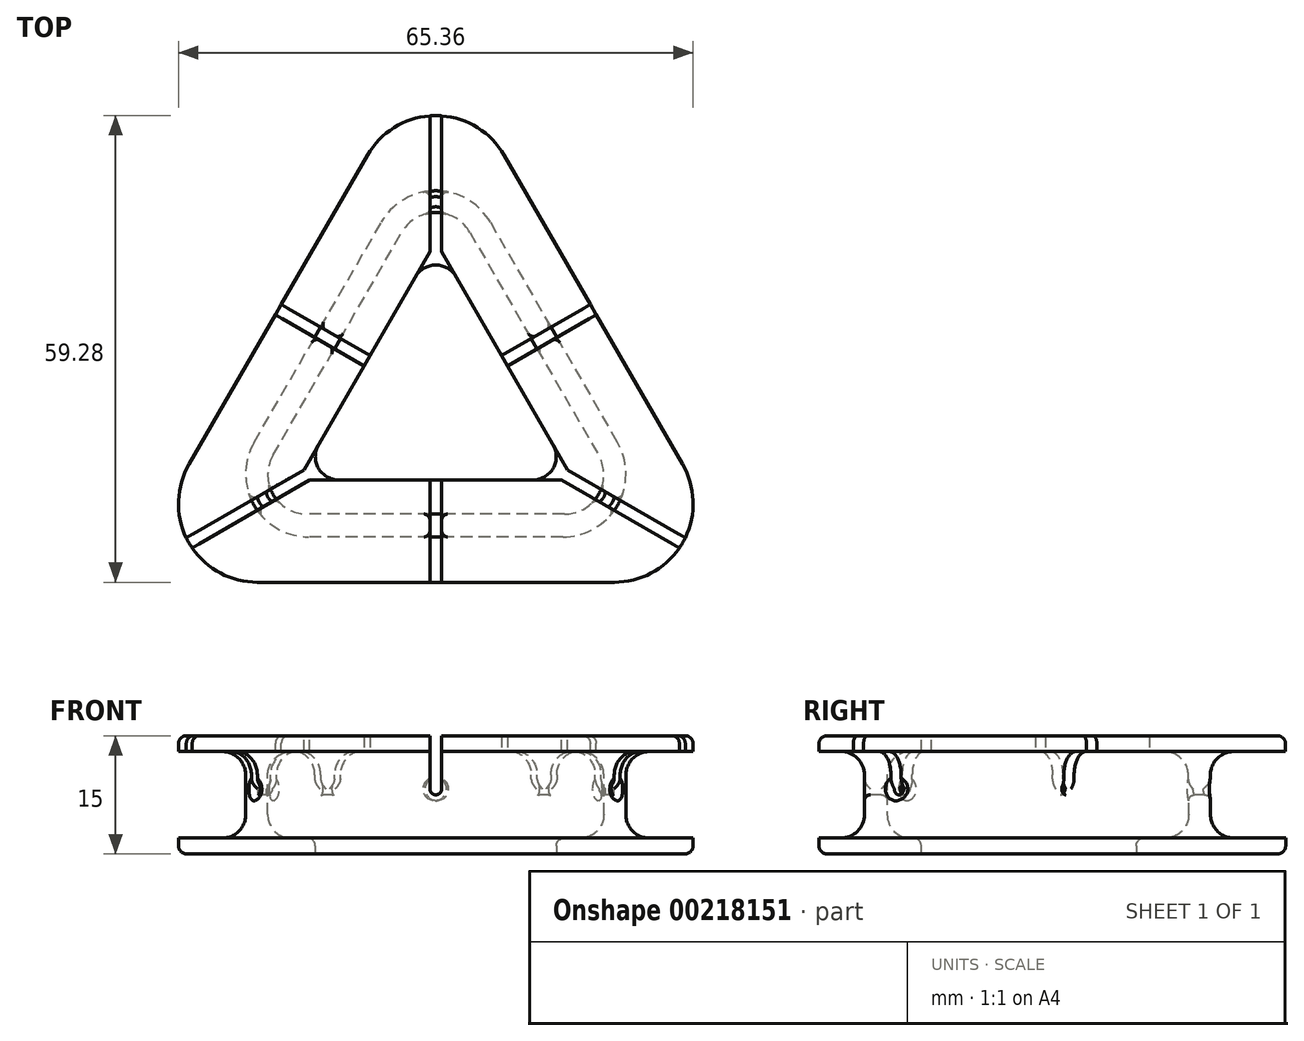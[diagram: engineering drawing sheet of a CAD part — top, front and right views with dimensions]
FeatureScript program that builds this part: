
annotation { "Feature Type Name" : "Feature", "Feature Type Description" : "" }
export const myFeature = defineFeature(function(context is Context, id is Id, definition is map)
    precondition{}
    {
        {
            var Q0;
            Q0=qCreatedBy(makeId("Top.planeOp"),FACE);
            var sketch = newSketch(context, id + "F0", { "sketchPlane" : qUnion([Q0])});
            skCircle(sketch, "E0.cCircle", {"center": v(0, 0) * mm, "radius": 23.1 * mm, "construction": true});
            skLineSegment(sketch, "E0.0", {"start": v(40, -23.1) * mm, "end": v(-40, -23.1) * mm});
            skLineSegment(sketch, "E0.1", {"start": v(-40, -23.1) * mm, "end": v(0, 46.19) * mm});
            skLineSegment(sketch, "E0.2", {"start": v(0, 46.19) * mm, "end": v(40, -23.1) * mm});
            skPoint(sketch, "E0.0.midPoint", {"position": v(0, -23.1) * mm});
            skSolve(sketch);
        }
        {
            var Q0;
            Q0 = qSketchRegion(id + "F0", true);
            extrude(context, id + "F1", {"entities" : qUnion([Q0]), "offsetDistance" : 25 * mm, "depth" : 15 * mm, "symmetric" : true});
        }
        {
            var Q0;
            Q0=makeQuery(id+"F1.opExtrude","SWEPT_EDGE",EDGE,{"disambiguationData":[OSD([sQuery(id+"F0.wireOp",EDGE,"E0.1"),sQuery(id+"F0.wireOp",EDGE,"E0.2")])]});
            var Q1;
            Q1=makeQuery(id+"F1.opExtrude","SWEPT_EDGE",EDGE,{"disambiguationData":[OSD([sQuery(id+"F0.wireOp",EDGE,"E0.0"),sQuery(id+"F0.wireOp",EDGE,"E0.1")])]});
            var Q2;
            Q2=makeQuery(id+"F1.opExtrude","SWEPT_EDGE",EDGE,{"disambiguationData":[OSD([sQuery(id+"F0.wireOp",EDGE,"E0.0"),sQuery(id+"F0.wireOp",EDGE,"E0.2")])]});
            fillet(context, id + "F2", {"entities" : qUnion([Q0, Q1, Q2]), "radius" : 10 * mm, "tangentPropagation" : true, "allowEdgeOverflow" : false});
        }
        {
            var Q0;
            Q0=qCreatedBy(makeId("Top.planeOp"),FACE);
            var sketch = newSketch(context, id + "F3", { "sketchPlane" : qUnion([Q0])});
            skCircle(sketch, "E1.cCircle", {"center": v(0, 0) * mm, "radius": 17.32 * mm, "construction": true});
            skLineSegment(sketch, "E1.0", {"start": v(0, 34.64) * mm, "end": v(30, -17.32) * mm});
            skLineSegment(sketch, "E1.1", {"start": v(30, -17.32) * mm, "end": v(-30, -17.32) * mm});
            skLineSegment(sketch, "E1.2", {"start": v(-30, -17.32) * mm, "end": v(0, 34.64) * mm});
            skPoint(sketch, "E1.0.midPoint", {"position": v(15, 8.66) * mm});
            skCircle(sketch, "E2.cCircle", {"center": v(0, 0) * mm, "radius": 23.1 * mm, "construction": true});
            skLineSegment(sketch, "E2.0", {"start": v(40, -23.1) * mm, "end": v(-40, -23.1) * mm});
            skLineSegment(sketch, "E2.1", {"start": v(-40, -23.1) * mm, "end": v(0, 46.19) * mm});
            skLineSegment(sketch, "E2.2", {"start": v(0, 46.19) * mm, "end": v(40, -23.1) * mm});
            skPoint(sketch, "E2.0.midPoint", {"position": v(0, -23.1) * mm});
            skSolve(sketch);
        }
        {
            var Q0;
            Q0=makeQuery(id+"F3.imprint","IMPRINT",FACE,{"disambiguationData":[TD([[makeQuery(id+"F3.imprint","IMPRINT",EDGE,{"derivedFrom":sQuery(id+"F3.wireOp",EDGE,"E1.0")}),1.0]])]});
            extrude(context, id + "F4", {"entities" : qUnion([Q0]), "operationType" : NewBodyOperationType.REMOVE, "oppositeDirection" : true, "depth" : 11 * mm, "symmetric" : true});
        }
        {
            var Q0;
            Q0=qCreatedBy(makeId("Top.planeOp"),FACE);
            var sketch = newSketch(context, id + "F5", { "sketchPlane" : qUnion([Q0])});
            skCircle(sketch, "E3.cCircle", {"center": v(0, 0) * mm, "radius": 14.43 * mm, "construction": true});
            skLineSegment(sketch, "E3.0", {"start": v(25, -14.43) * mm, "end": v(-25, -14.43) * mm});
            skLineSegment(sketch, "E3.1", {"start": v(-25, -14.43) * mm, "end": v(0, 28.87) * mm});
            skLineSegment(sketch, "E3.2", {"start": v(0, 28.87) * mm, "end": v(25, -14.43) * mm});
            skPoint(sketch, "E3.0.midPoint", {"position": v(0, -14.43) * mm});
            skSolve(sketch);
        }
        {
            var Q0;
            Q0 = qSketchRegion(id + "F5", true);
            extrude(context, id + "F6", {"entities" : qUnion([Q0]), "operationType" : NewBodyOperationType.REMOVE, "depth" : 11 * mm, "symmetric" : true});
        }
        {
            var Q0;
            Q0=makeQuery(id+"F1.opExtrude","CAP_FACE",FACE,{"disambiguationData":[OSD([sQuery(id+"F0.wireOp",EDGE,"E0.0"),sQuery(id+"F0.wireOp",EDGE,"E0.1"),sQuery(id+"F0.wireOp",EDGE,"E0.2")])],"isStart":false});
            var sketch = newSketch(context, id + "F7", { "sketchPlane" : qUnion([Q0])});
            skCircle(sketch, "E4.cCircle", {"center": v(0, 0) * mm, "radius": 10.1 * mm, "construction": true});
            skLineSegment(sketch, "E4.0", {"start": v(17.5, -10.1) * mm, "end": v(-17.5, -10.1) * mm});
            skLineSegment(sketch, "E4.1", {"start": v(-17.5, -10.1) * mm, "end": v(0, 20.2) * mm});
            skLineSegment(sketch, "E4.2", {"start": v(0, 20.2) * mm, "end": v(17.5, -10.1) * mm});
            skPoint(sketch, "E4.0.midPoint", {"position": v(0, -10.1) * mm});
            skSolve(sketch);
        }
        {
            var Q0;
            Q0=makeQuery(id+"F7.imprint","IMPRINT",FACE,{"disambiguationData":[TD([[makeQuery(id+"F7.imprint","IMPRINT",EDGE,{"derivedFrom":sQuery(id+"F7.wireOp",EDGE,"E4.0")}),-1.0]])]});
            var Q1;
            Q1=makeQuery(id+"F1.opExtrude","CAP_FACE",FACE,{"disambiguationData":[OSD([sQuery(id+"F0.wireOp",EDGE,"E0.0"),sQuery(id+"F0.wireOp",EDGE,"E0.1"),sQuery(id+"F0.wireOp",EDGE,"E0.2")])],"isStart":true});
            extrude(context, id + "F8", {"entities" : qUnion([Q0]), "operationType" : NewBodyOperationType.REMOVE, "endBound" : BoundingType.UP_TO_SURFACE, "oppositeDirection" : true, "endBoundEntityFace" : qUnion([Q1]), "depth" : 25 * mm});
        }
        {
            var Q0;
            Q0=makeQuery(id+"F6.boolean.opBoolean","COPY",EDGE,{"derivedFrom":makeQuery(id+"F6.opExtrude","SWEPT_EDGE",EDGE,{"disambiguationData":[OSD([sQuery(id+"F5.wireOp",EDGE,"E3.1"),sQuery(id+"F5.wireOp",EDGE,"E3.2")])]})});
            var Q1;
            Q1=makeQuery(id+"F6.boolean.opBoolean","COPY",EDGE,{"derivedFrom":makeQuery(id+"F6.opExtrude","SWEPT_EDGE",EDGE,{"disambiguationData":[OSD([sQuery(id+"F5.wireOp",EDGE,"E3.0"),sQuery(id+"F5.wireOp",EDGE,"E3.1")])]})});
            var Q2;
            Q2=makeQuery(id+"F6.boolean.opBoolean","COPY",EDGE,{"derivedFrom":makeQuery(id+"F6.opExtrude","SWEPT_EDGE",EDGE,{"disambiguationData":[OSD([sQuery(id+"F5.wireOp",EDGE,"E3.0"),sQuery(id+"F5.wireOp",EDGE,"E3.2")])]})});
            fillet(context, id + "F9", {"entities" : qUnion([Q0, Q1, Q2]), "radius" : 5 * mm, "tangentPropagation" : true, "allowEdgeOverflow" : false});
        }
        {
            var Q0;
            Q0=makeQuery(id+"F4.boolean.opBoolean","COPY",EDGE,{"derivedFrom":makeQuery(id+"F4.opExtrude","SWEPT_EDGE",EDGE,{"disambiguationData":[OSD([sQuery(id+"F3.wireOp",EDGE,"E1.0"),sQuery(id+"F3.wireOp",EDGE,"E1.1")])]})});
            var Q1;
            Q1=makeQuery(id+"F4.boolean.opBoolean","COPY",EDGE,{"derivedFrom":makeQuery(id+"F4.opExtrude","SWEPT_EDGE",EDGE,{"disambiguationData":[OSD([sQuery(id+"F3.wireOp",EDGE,"E1.0"),sQuery(id+"F3.wireOp",EDGE,"E1.2")])]})});
            var Q2;
            Q2=makeQuery(id+"F4.boolean.opBoolean","COPY",EDGE,{"derivedFrom":makeQuery(id+"F4.opExtrude","SWEPT_EDGE",EDGE,{"disambiguationData":[OSD([sQuery(id+"F3.wireOp",EDGE,"E1.1"),sQuery(id+"F3.wireOp",EDGE,"E1.2")])]})});
            fillet(context, id + "F10", {"entities" : qUnion([Q0, Q1, Q2]), "radius" : 8 * mm, "tangentPropagation" : true, "allowEdgeOverflow" : false});
        }
        {
            var Q0;
            Q0=makeQuery(id+"F6.boolean.opBoolean","COPY",FACE,{"derivedFrom":makeQuery(id+"F6.opExtrude","SWEPT_FACE",FACE,{"disambiguationData":[OSD([sQuery(id+"F5.wireOp",EDGE,"E3.2")])]})});
            var Q1;
            Q1=makeQuery(id+"F4.boolean.opBoolean","COPY",FACE,{"derivedFrom":makeQuery(id+"F4.opExtrude","SWEPT_FACE",FACE,{"disambiguationData":[OSD([sQuery(id+"F3.wireOp",EDGE,"E1.2")])]})});
            fillet(context, id + "F11", {"entities" : qUnion([Q0, Q1]), "radius" : 3 * mm, "tangentPropagation" : true, "allowEdgeOverflow" : false});
        }
        {
            var Q0;
            Q0=makeQuery(id+"F1.opExtrude","CAP_FACE",FACE,{"disambiguationData":[OSD([sQuery(id+"F0.wireOp",EDGE,"E0.0"),sQuery(id+"F0.wireOp",EDGE,"E0.1"),sQuery(id+"F0.wireOp",EDGE,"E0.2")])],"isStart":false});
            var sketch = newSketch(context, id + "F12", { "sketchPlane" : qUnion([Q0])});
            skLineSegment(sketch, "E5.bottom", {"start": v(-0.75, 36.19) * mm, "end": v(0.75, 36.19) * mm});
            skLineSegment(sketch, "E5.top", {"start": v(-0.75, -23.1) * mm, "end": v(0.75, -23.1) * mm});
            skLineSegment(sketch, "E5.left", {"start": v(-0.75, 36.19) * mm, "end": v(-0.75, -23.1) * mm});
            skLineSegment(sketch, "E5.right", {"start": v(0.75, 36.19) * mm, "end": v(0.75, -23.1) * mm});
            skLineSegment(sketch, "E6.bottom", {"start": v(-19.62, 12.2) * mm, "end": v(31.71, -17.44) * mm});
            skLineSegment(sketch, "E6.top", {"start": v(-20.38, 10.9) * mm, "end": v(30.96, -18.74) * mm});
            skLineSegment(sketch, "E6.left", {"start": v(-19.62, 12.2) * mm, "end": v(-20.37, 10.9) * mm});
            skLineSegment(sketch, "E6.right", {"start": v(31.71, -17.44) * mm, "end": v(30.96, -18.74) * mm});
            skLineSegment(sketch, "E7.bottom", {"start": v(19.62, 12.2) * mm, "end": v(-31.71, -17.44) * mm});
            skLineSegment(sketch, "E7.top", {"start": v(20.37, 10.9) * mm, "end": v(-30.96, -18.74) * mm});
            skLineSegment(sketch, "E7.left", {"start": v(19.62, 12.2) * mm, "end": v(20.37, 10.9) * mm});
            skLineSegment(sketch, "E7.right", {"start": v(-31.71, -17.44) * mm, "end": v(-30.96, -18.74) * mm});
            skLineSegment(sketch, "E8", {"start": v(20, 11.55) * mm, "end": v(-31.34, -18.1) * mm, "construction": true});
            skLineSegment(sketch, "E9", {"start": v(-20, 11.55) * mm, "end": v(31.34, -18.1) * mm, "construction": true});
            skSolve(sketch);
        }
        {
            var Q0;
            Q0 = qSketchRegion(id + "F12", true);
            extrude(context, id + "F13", {"entities" : qUnion([Q0]), "operationType" : NewBodyOperationType.REMOVE, "oppositeDirection" : true, "depth" : 7.5 * mm});
        }
        {
            var Q0;
            {var subQ0=sQuery(id+"F12.wireOp",EDGE,"E5.right");var subQ1=sQuery(id+"F0.wireOp",EDGE,"E0.2");var subQ2=sQuery(id+"F0.wireOp",EDGE,"E0.1");var subQ3=makeQuery(id+"F1.opExtrude","CAP_FACE",FACE,{"disambiguationData":[OSD([sQuery(id+"F0.wireOp",EDGE,"E0.0"),subQ2,subQ1])],"isStart":false});var subQ7=makeQuery(id+"F12.imprint","INTERSECT",VERTEX,{"derivedFrom":[makeQuery(id+"F2.opFillet","BLEND_EDGE",EDGE,{"blendedFrom":[makeQuery(id+"F1.opExtrude","SWEPT_EDGE",EDGE,{"disambiguationData":[OSD([subQ2,subQ1])]}),subQ3],"blendedInto":[subQ3]}),subQ0]});Q0=makeQuery(id+"F13.boolean.opBoolean","COPY",EDGE,{"derivedFrom":makeQuery(id+"F13.opExtrude","CAP_EDGE",EDGE,{"disambiguationData":[OSD([subQ0]),TDD([makeQuery(id+"F12.imprint","IMPRINT",EDGE,{"disambiguationData":[TD([[makeQuery(id+"F12.imprint","INTERSECT",VERTEX,{"derivedFrom":[sQuery(id+"F12.wireOp",EDGE,"E5.bottom"),subQ0]}),-1.0]])],"derivedFrom":subQ0}),makeQuery(id+"F12.imprint","IMPRINT",EDGE,{"disambiguationData":[TD([[subQ7,-1.0]])],"derivedFrom":subQ0}),makeQuery(id+"F12.imprint","IMPRINT",EDGE,{"disambiguationData":[TD([[makeQuery(id+"F12.imprint","INTERSECT",VERTEX,{"derivedFrom":[subQ0,sQuery(id+"F12.wireOp",EDGE,"E7.bottom")]}),1.0]])],"derivedFrom":subQ0})])],"isStart":true})});}
            var Q1;
            {var subQ0=sQuery(id+"F12.wireOp",EDGE,"E5.left");var subQ1=sQuery(id+"F0.wireOp",EDGE,"E0.2");var subQ2=sQuery(id+"F0.wireOp",EDGE,"E0.1");var subQ3=makeQuery(id+"F1.opExtrude","CAP_FACE",FACE,{"disambiguationData":[OSD([sQuery(id+"F0.wireOp",EDGE,"E0.0"),subQ2,subQ1])],"isStart":false});var subQ7=makeQuery(id+"F12.imprint","INTERSECT",VERTEX,{"derivedFrom":[makeQuery(id+"F2.opFillet","BLEND_EDGE",EDGE,{"blendedFrom":[makeQuery(id+"F1.opExtrude","SWEPT_EDGE",EDGE,{"disambiguationData":[OSD([subQ2,subQ1])]}),subQ3],"blendedInto":[subQ3]}),subQ0]});Q1=makeQuery(id+"F13.boolean.opBoolean","COPY",EDGE,{"derivedFrom":makeQuery(id+"F13.opExtrude","CAP_EDGE",EDGE,{"disambiguationData":[OSD([subQ0]),TDD([makeQuery(id+"F12.imprint","IMPRINT",EDGE,{"disambiguationData":[TD([[makeQuery(id+"F12.imprint","INTERSECT",VERTEX,{"derivedFrom":[sQuery(id+"F12.wireOp",EDGE,"E5.bottom"),subQ0]}),-1.0]])],"derivedFrom":subQ0}),makeQuery(id+"F12.imprint","IMPRINT",EDGE,{"disambiguationData":[TD([[subQ7,-1.0]])],"derivedFrom":subQ0}),makeQuery(id+"F12.imprint","IMPRINT",EDGE,{"disambiguationData":[TD([[makeQuery(id+"F12.imprint","INTERSECT",VERTEX,{"derivedFrom":[subQ0,sQuery(id+"F12.wireOp",EDGE,"E6.bottom")]}),1.0]])],"derivedFrom":subQ0})])],"isStart":true})});}
            var Q2;
            {var subQ0=sQuery(id+"F5.wireOp",EDGE,"E3.2");var subQ1=sQuery(id+"F5.wireOp",EDGE,"E3.1");var subQ2=sQuery(id+"F12.wireOp",EDGE,"E6.bottom");var subQ3=sQuery(id+"F12.wireOp",EDGE,"E5.left");var subQ13=sQuery(id+"F12.wireOp",EDGE,"E5.bottom");var subQ14=sQuery(id+"F12.wireOp",EDGE,"E7.bottom");var subQ15=sQuery(id+"F12.wireOp",EDGE,"E5.right");Q2=makeQuery(id+"F13.boolean.opBoolean","COPY",FACE,{"disambiguationData":[TD([makeQuery(id+"F9.opFillet","BLEND_FACE",FACE,{"disambiguationData":[OSD([subQ1,subQ0])]})])],"derivedFrom":makeQuery(id+"F13.opExtrude","CAP_FACE",FACE,{"disambiguationData":[OSD([subQ13,sQuery(id+"F12.wireOp",EDGE,"E5.top"),subQ3,subQ15,subQ2,sQuery(id+"F12.wireOp",EDGE,"E6.top"),sQuery(id+"F12.wireOp",EDGE,"E6.left"),sQuery(id+"F12.wireOp",EDGE,"E6.right"),subQ14,sQuery(id+"F12.wireOp",EDGE,"E7.top"),sQuery(id+"F12.wireOp",EDGE,"E7.left"),sQuery(id+"F12.wireOp",EDGE,"E7.right")])],"isStart":false})});}
            var Q3;
            {var subQ0=sQuery(id+"F12.wireOp",EDGE,"E6.bottom");var subQ1=makeQuery(id+"F12.imprint","INTERSECT",VERTEX,{"derivedFrom":[makeQuery(id+"F8.boolean.opBoolean","COPY",EDGE,{"derivedFrom":makeQuery(id+"F8.opExtrude","CAP_EDGE",EDGE,{"disambiguationData":[OSD([sQuery(id+"F7.wireOp",EDGE,"E4.1")])],"isStart":true})}),subQ0]});Q3=makeQuery(id+"F13.boolean.opBoolean","COPY",EDGE,{"derivedFrom":makeQuery(id+"F13.opExtrude","CAP_EDGE",EDGE,{"disambiguationData":[OSD([subQ0]),TDD([makeQuery(id+"F12.imprint","IMPRINT",EDGE,{"disambiguationData":[TD([[subQ1,1.0]])],"derivedFrom":subQ0}),makeQuery(id+"F12.imprint","IMPRINT",EDGE,{"disambiguationData":[TD([[makeQuery(id+"F12.imprint","INTERSECT",VERTEX,{"derivedFrom":[sQuery(id+"F12.wireOp",EDGE,"E5.left"),subQ0]}),1.0]])],"derivedFrom":subQ0})])],"isStart":true})});}
            var Q4;
            {var subQ0=sQuery(id+"F12.wireOp",EDGE,"E6.top");var subQ1=makeQuery(id+"F12.imprint","INTERSECT",VERTEX,{"derivedFrom":[makeQuery(id+"F8.boolean.opBoolean","COPY",EDGE,{"derivedFrom":makeQuery(id+"F8.opExtrude","CAP_EDGE",EDGE,{"disambiguationData":[OSD([sQuery(id+"F7.wireOp",EDGE,"E4.1")])],"isStart":true})}),subQ0]});Q4=makeQuery(id+"F13.boolean.opBoolean","COPY",EDGE,{"derivedFrom":makeQuery(id+"F13.opExtrude","CAP_EDGE",EDGE,{"disambiguationData":[OSD([subQ0]),TDD([makeQuery(id+"F12.imprint","IMPRINT",EDGE,{"disambiguationData":[TD([[subQ1,1.0]])],"derivedFrom":subQ0}),makeQuery(id+"F12.imprint","IMPRINT",EDGE,{"disambiguationData":[TD([[makeQuery(id+"F12.imprint","INTERSECT",VERTEX,{"derivedFrom":[subQ0,sQuery(id+"F12.wireOp",EDGE,"E7.bottom")]}),1.0]])],"derivedFrom":subQ0})])],"isStart":true})});}
            var Q5;
            {var subQ0=sQuery(id+"F12.wireOp",EDGE,"E7.bottom");var subQ1=sQuery(id+"F12.wireOp",EDGE,"E6.top");var subQ4=sQuery(id+"F12.wireOp",EDGE,"E6.left");var subQ6=sQuery(id+"F12.wireOp",EDGE,"E6.bottom");var subQ7=sQuery(id+"F12.wireOp",EDGE,"E5.left");Q5=makeQuery(id+"F13.boolean.opBoolean","COPY",FACE,{"disambiguationData":[TD([makeQuery(id+"F4.boolean.opBoolean","COPY",FACE,{"derivedFrom":makeQuery(id+"F4.opExtrude","SWEPT_FACE",FACE,{"disambiguationData":[OSD([sQuery(id+"F3.wireOp",EDGE,"E1.2")])]})})])],"derivedFrom":makeQuery(id+"F13.opExtrude","CAP_FACE",FACE,{"disambiguationData":[OSD([sQuery(id+"F12.wireOp",EDGE,"E5.bottom"),sQuery(id+"F12.wireOp",EDGE,"E5.top"),subQ7,sQuery(id+"F12.wireOp",EDGE,"E5.right"),subQ6,subQ1,subQ4,sQuery(id+"F12.wireOp",EDGE,"E6.right"),subQ0,sQuery(id+"F12.wireOp",EDGE,"E7.top"),sQuery(id+"F12.wireOp",EDGE,"E7.left"),sQuery(id+"F12.wireOp",EDGE,"E7.right")])],"isStart":false})});}
            var Q6;
            {var subQ0=sQuery(id+"F12.wireOp",EDGE,"E7.bottom");var subQ1=sQuery(id+"F0.wireOp",EDGE,"E0.1");var subQ2=sQuery(id+"F0.wireOp",EDGE,"E0.0");var subQ3=makeQuery(id+"F1.opExtrude","CAP_FACE",FACE,{"disambiguationData":[OSD([subQ2,subQ1,sQuery(id+"F0.wireOp",EDGE,"E0.2")])],"isStart":false});var subQ4=makeQuery(id+"F12.imprint","INTERSECT",VERTEX,{"derivedFrom":[makeQuery(id+"F2.opFillet","BLEND_EDGE",EDGE,{"blendedFrom":[makeQuery(id+"F1.opExtrude","SWEPT_EDGE",EDGE,{"disambiguationData":[OSD([subQ2,subQ1])]}),subQ3],"blendedInto":[subQ3]}),subQ0]});Q6=makeQuery(id+"F13.boolean.opBoolean","COPY",EDGE,{"derivedFrom":makeQuery(id+"F13.opExtrude","CAP_EDGE",EDGE,{"disambiguationData":[OSD([subQ0]),TDD([makeQuery(id+"F12.imprint","IMPRINT",EDGE,{"disambiguationData":[TD([[makeQuery(id+"F12.imprint","INTERSECT",VERTEX,{"derivedFrom":[sQuery(id+"F12.wireOp",EDGE,"E6.top"),subQ0]}),-1.0]])],"derivedFrom":subQ0}),makeQuery(id+"F12.imprint","IMPRINT",EDGE,{"disambiguationData":[TD([[subQ4,1.0]])],"derivedFrom":subQ0}),makeQuery(id+"F12.imprint","IMPRINT",EDGE,{"disambiguationData":[TD([[makeQuery(id+"F12.imprint","INTERSECT",VERTEX,{"derivedFrom":[subQ0,sQuery(id+"F12.wireOp",EDGE,"E7.right")]}),1.0]])],"derivedFrom":subQ0})])],"isStart":true})});}
            var Q7;
            {var subQ0=sQuery(id+"F12.wireOp",EDGE,"E7.top");var subQ1=sQuery(id+"F0.wireOp",EDGE,"E0.1");var subQ2=sQuery(id+"F0.wireOp",EDGE,"E0.0");var subQ3=makeQuery(id+"F1.opExtrude","CAP_FACE",FACE,{"disambiguationData":[OSD([subQ2,subQ1,sQuery(id+"F0.wireOp",EDGE,"E0.2")])],"isStart":false});var subQ4=makeQuery(id+"F12.imprint","INTERSECT",VERTEX,{"derivedFrom":[makeQuery(id+"F2.opFillet","BLEND_EDGE",EDGE,{"blendedFrom":[makeQuery(id+"F1.opExtrude","SWEPT_EDGE",EDGE,{"disambiguationData":[OSD([subQ2,subQ1])]}),subQ3],"blendedInto":[subQ3]}),subQ0]});Q7=makeQuery(id+"F13.boolean.opBoolean","COPY",EDGE,{"derivedFrom":makeQuery(id+"F13.opExtrude","CAP_EDGE",EDGE,{"disambiguationData":[OSD([subQ0]),TDD([makeQuery(id+"F12.imprint","IMPRINT",EDGE,{"disambiguationData":[TD([[makeQuery(id+"F12.imprint","INTERSECT",VERTEX,{"derivedFrom":[sQuery(id+"F12.wireOp",EDGE,"E5.left"),subQ0]}),-1.0]])],"derivedFrom":subQ0}),makeQuery(id+"F12.imprint","IMPRINT",EDGE,{"disambiguationData":[TD([[subQ4,1.0]])],"derivedFrom":subQ0}),makeQuery(id+"F12.imprint","IMPRINT",EDGE,{"disambiguationData":[TD([[makeQuery(id+"F12.imprint","INTERSECT",VERTEX,{"derivedFrom":[subQ0,sQuery(id+"F12.wireOp",EDGE,"E7.right")]}),1.0]])],"derivedFrom":subQ0})])],"isStart":true})});}
            var Q8;
            {var subQ0=sQuery(id+"F5.wireOp",EDGE,"E3.1");var subQ1=sQuery(id+"F5.wireOp",EDGE,"E3.0");var subQ2=sQuery(id+"F12.wireOp",EDGE,"E7.right");var subQ3=sQuery(id+"F12.wireOp",EDGE,"E7.top");var subQ13=sQuery(id+"F12.wireOp",EDGE,"E5.left");var subQ14=sQuery(id+"F12.wireOp",EDGE,"E7.bottom");var subQ17=sQuery(id+"F12.wireOp",EDGE,"E6.top");Q8=makeQuery(id+"F13.boolean.opBoolean","COPY",FACE,{"disambiguationData":[TD([makeQuery(id+"F9.opFillet","BLEND_FACE",FACE,{"disambiguationData":[OSD([subQ1,subQ0])]})])],"derivedFrom":makeQuery(id+"F13.opExtrude","CAP_FACE",FACE,{"disambiguationData":[OSD([sQuery(id+"F12.wireOp",EDGE,"E5.bottom"),sQuery(id+"F12.wireOp",EDGE,"E5.top"),subQ13,sQuery(id+"F12.wireOp",EDGE,"E5.right"),sQuery(id+"F12.wireOp",EDGE,"E6.bottom"),subQ17,sQuery(id+"F12.wireOp",EDGE,"E6.left"),sQuery(id+"F12.wireOp",EDGE,"E6.right"),subQ14,subQ3,sQuery(id+"F12.wireOp",EDGE,"E7.left"),subQ2])],"isStart":false})});}
            var Q9;
            {var subQ0=sQuery(id+"F12.wireOp",EDGE,"E5.left");var subQ1=sQuery(id+"F12.wireOp",EDGE,"E5.top");var subQ5=sQuery(id+"F12.wireOp",EDGE,"E7.top");var subQ6=sQuery(id+"F12.wireOp",EDGE,"E5.right");var subQ8=sQuery(id+"F12.wireOp",EDGE,"E6.top");Q9=makeQuery(id+"F13.boolean.opBoolean","COPY",FACE,{"disambiguationData":[TD([makeQuery(id+"F4.boolean.opBoolean","COPY",FACE,{"derivedFrom":makeQuery(id+"F4.opExtrude","SWEPT_FACE",FACE,{"disambiguationData":[OSD([sQuery(id+"F3.wireOp",EDGE,"E1.1")])]})})])],"derivedFrom":makeQuery(id+"F13.opExtrude","CAP_FACE",FACE,{"disambiguationData":[OSD([sQuery(id+"F12.wireOp",EDGE,"E5.bottom"),subQ1,subQ0,subQ6,sQuery(id+"F12.wireOp",EDGE,"E6.bottom"),subQ8,sQuery(id+"F12.wireOp",EDGE,"E6.left"),sQuery(id+"F12.wireOp",EDGE,"E6.right"),sQuery(id+"F12.wireOp",EDGE,"E7.bottom"),subQ5,sQuery(id+"F12.wireOp",EDGE,"E7.left"),sQuery(id+"F12.wireOp",EDGE,"E7.right")])],"isStart":false})});}
            var Q10;
            {var subQ0=sQuery(id+"F12.wireOp",EDGE,"E5.right");var subQ1=makeQuery(id+"F12.imprint","INTERSECT",VERTEX,{"derivedFrom":[makeQuery(id+"F8.boolean.opBoolean","COPY",EDGE,{"derivedFrom":makeQuery(id+"F8.opExtrude","CAP_EDGE",EDGE,{"disambiguationData":[OSD([sQuery(id+"F7.wireOp",EDGE,"E4.0")])],"isStart":true})}),subQ0]});Q10=makeQuery(id+"F13.boolean.opBoolean","COPY",EDGE,{"derivedFrom":makeQuery(id+"F13.opExtrude","CAP_EDGE",EDGE,{"disambiguationData":[OSD([subQ0]),TDD([makeQuery(id+"F12.imprint","IMPRINT",EDGE,{"disambiguationData":[TD([[makeQuery(id+"F12.imprint","INTERSECT",VERTEX,{"derivedFrom":[subQ0,sQuery(id+"F12.wireOp",EDGE,"E6.top")]}),-1.0]])],"derivedFrom":subQ0}),makeQuery(id+"F12.imprint","IMPRINT",EDGE,{"disambiguationData":[TD([[subQ1,-1.0]])],"derivedFrom":subQ0})])],"isStart":true})});}
            var Q11;
            {var subQ0=sQuery(id+"F12.wireOp",EDGE,"E5.left");var subQ1=makeQuery(id+"F12.imprint","INTERSECT",VERTEX,{"derivedFrom":[makeQuery(id+"F8.boolean.opBoolean","COPY",EDGE,{"derivedFrom":makeQuery(id+"F8.opExtrude","CAP_EDGE",EDGE,{"disambiguationData":[OSD([sQuery(id+"F7.wireOp",EDGE,"E4.0")])],"isStart":true})}),subQ0]});Q11=makeQuery(id+"F13.boolean.opBoolean","COPY",EDGE,{"derivedFrom":makeQuery(id+"F13.opExtrude","CAP_EDGE",EDGE,{"disambiguationData":[OSD([subQ0]),TDD([makeQuery(id+"F12.imprint","IMPRINT",EDGE,{"disambiguationData":[TD([[makeQuery(id+"F12.imprint","INTERSECT",VERTEX,{"derivedFrom":[subQ0,sQuery(id+"F12.wireOp",EDGE,"E7.top")]}),-1.0]])],"derivedFrom":subQ0}),makeQuery(id+"F12.imprint","IMPRINT",EDGE,{"disambiguationData":[TD([[subQ1,-1.0]])],"derivedFrom":subQ0})])],"isStart":true})});}
            var Q12;
            {var subQ0=sQuery(id+"F12.wireOp",EDGE,"E6.bottom");var subQ1=sQuery(id+"F0.wireOp",EDGE,"E0.2");var subQ2=sQuery(id+"F0.wireOp",EDGE,"E0.0");var subQ3=makeQuery(id+"F1.opExtrude","CAP_FACE",FACE,{"disambiguationData":[OSD([subQ2,sQuery(id+"F0.wireOp",EDGE,"E0.1"),subQ1])],"isStart":false});var subQ4=makeQuery(id+"F12.imprint","INTERSECT",VERTEX,{"derivedFrom":[makeQuery(id+"F2.opFillet","BLEND_EDGE",EDGE,{"blendedFrom":[makeQuery(id+"F1.opExtrude","SWEPT_EDGE",EDGE,{"disambiguationData":[OSD([subQ2,subQ1])]}),subQ3],"blendedInto":[subQ3]}),subQ0]});Q12=makeQuery(id+"F13.boolean.opBoolean","COPY",EDGE,{"derivedFrom":makeQuery(id+"F13.opExtrude","CAP_EDGE",EDGE,{"disambiguationData":[OSD([subQ0]),TDD([makeQuery(id+"F12.imprint","IMPRINT",EDGE,{"disambiguationData":[TD([[makeQuery(id+"F12.imprint","INTERSECT",VERTEX,{"derivedFrom":[subQ0,sQuery(id+"F12.wireOp",EDGE,"E7.top")]}),-1.0]])],"derivedFrom":subQ0}),makeQuery(id+"F12.imprint","IMPRINT",EDGE,{"disambiguationData":[TD([[subQ4,1.0]])],"derivedFrom":subQ0}),makeQuery(id+"F12.imprint","IMPRINT",EDGE,{"disambiguationData":[TD([[makeQuery(id+"F12.imprint","INTERSECT",VERTEX,{"derivedFrom":[subQ0,sQuery(id+"F12.wireOp",EDGE,"E6.right")]}),1.0]])],"derivedFrom":subQ0})])],"isStart":true})});}
            var Q13;
            {var subQ0=sQuery(id+"F5.wireOp",EDGE,"E3.2");var subQ1=sQuery(id+"F5.wireOp",EDGE,"E3.0");var subQ2=sQuery(id+"F12.wireOp",EDGE,"E6.right");var subQ3=sQuery(id+"F12.wireOp",EDGE,"E6.bottom");var subQ13=sQuery(id+"F12.wireOp",EDGE,"E7.top");var subQ14=sQuery(id+"F12.wireOp",EDGE,"E6.top");var subQ17=sQuery(id+"F12.wireOp",EDGE,"E5.right");Q13=makeQuery(id+"F13.boolean.opBoolean","COPY",FACE,{"disambiguationData":[TD([makeQuery(id+"F9.opFillet","BLEND_FACE",FACE,{"disambiguationData":[OSD([subQ1,subQ0])]})])],"derivedFrom":makeQuery(id+"F13.opExtrude","CAP_FACE",FACE,{"disambiguationData":[OSD([sQuery(id+"F12.wireOp",EDGE,"E5.bottom"),sQuery(id+"F12.wireOp",EDGE,"E5.top"),sQuery(id+"F12.wireOp",EDGE,"E5.left"),subQ17,subQ3,subQ14,sQuery(id+"F12.wireOp",EDGE,"E6.left"),subQ2,sQuery(id+"F12.wireOp",EDGE,"E7.bottom"),subQ13,sQuery(id+"F12.wireOp",EDGE,"E7.left"),sQuery(id+"F12.wireOp",EDGE,"E7.right")])],"isStart":false})});}
            var Q14;
            {var subQ0=sQuery(id+"F12.wireOp",EDGE,"E6.top");var subQ1=sQuery(id+"F0.wireOp",EDGE,"E0.2");var subQ2=sQuery(id+"F0.wireOp",EDGE,"E0.0");var subQ3=makeQuery(id+"F1.opExtrude","CAP_FACE",FACE,{"disambiguationData":[OSD([subQ2,sQuery(id+"F0.wireOp",EDGE,"E0.1"),subQ1])],"isStart":false});var subQ4=makeQuery(id+"F12.imprint","INTERSECT",VERTEX,{"derivedFrom":[makeQuery(id+"F2.opFillet","BLEND_EDGE",EDGE,{"blendedFrom":[makeQuery(id+"F1.opExtrude","SWEPT_EDGE",EDGE,{"disambiguationData":[OSD([subQ2,subQ1])]}),subQ3],"blendedInto":[subQ3]}),subQ0]});Q14=makeQuery(id+"F13.boolean.opBoolean","COPY",EDGE,{"derivedFrom":makeQuery(id+"F13.opExtrude","CAP_EDGE",EDGE,{"disambiguationData":[OSD([subQ0]),TDD([makeQuery(id+"F12.imprint","IMPRINT",EDGE,{"disambiguationData":[TD([[makeQuery(id+"F12.imprint","INTERSECT",VERTEX,{"derivedFrom":[sQuery(id+"F12.wireOp",EDGE,"E5.right"),subQ0]}),-1.0]])],"derivedFrom":subQ0}),makeQuery(id+"F12.imprint","IMPRINT",EDGE,{"disambiguationData":[TD([[subQ4,1.0]])],"derivedFrom":subQ0}),makeQuery(id+"F12.imprint","IMPRINT",EDGE,{"disambiguationData":[TD([[makeQuery(id+"F12.imprint","INTERSECT",VERTEX,{"derivedFrom":[subQ0,sQuery(id+"F12.wireOp",EDGE,"E6.right")]}),1.0]])],"derivedFrom":subQ0})])],"isStart":true})});}
            var Q15;
            {var subQ0=sQuery(id+"F12.wireOp",EDGE,"E7.bottom");var subQ1=sQuery(id+"F12.wireOp",EDGE,"E5.right");var subQ4=sQuery(id+"F12.wireOp",EDGE,"E7.left");var subQ6=sQuery(id+"F12.wireOp",EDGE,"E7.top");var subQ7=sQuery(id+"F12.wireOp",EDGE,"E6.bottom");Q15=makeQuery(id+"F13.boolean.opBoolean","COPY",FACE,{"disambiguationData":[TD([makeQuery(id+"F4.boolean.opBoolean","COPY",FACE,{"derivedFrom":makeQuery(id+"F4.opExtrude","SWEPT_FACE",FACE,{"disambiguationData":[OSD([sQuery(id+"F3.wireOp",EDGE,"E1.0")])]})})])],"derivedFrom":makeQuery(id+"F13.opExtrude","CAP_FACE",FACE,{"disambiguationData":[OSD([sQuery(id+"F12.wireOp",EDGE,"E5.bottom"),sQuery(id+"F12.wireOp",EDGE,"E5.top"),sQuery(id+"F12.wireOp",EDGE,"E5.left"),subQ1,subQ7,sQuery(id+"F12.wireOp",EDGE,"E6.top"),sQuery(id+"F12.wireOp",EDGE,"E6.left"),sQuery(id+"F12.wireOp",EDGE,"E6.right"),subQ0,subQ6,subQ4,sQuery(id+"F12.wireOp",EDGE,"E7.right")])],"isStart":false})});}
            var Q16;
            {var subQ0=sQuery(id+"F12.wireOp",EDGE,"E7.bottom");var subQ1=makeQuery(id+"F12.imprint","INTERSECT",VERTEX,{"derivedFrom":[makeQuery(id+"F8.boolean.opBoolean","COPY",EDGE,{"derivedFrom":makeQuery(id+"F8.opExtrude","CAP_EDGE",EDGE,{"disambiguationData":[OSD([sQuery(id+"F7.wireOp",EDGE,"E4.2")])],"isStart":true})}),subQ0]});Q16=makeQuery(id+"F13.boolean.opBoolean","COPY",EDGE,{"derivedFrom":makeQuery(id+"F13.opExtrude","CAP_EDGE",EDGE,{"disambiguationData":[OSD([subQ0]),TDD([makeQuery(id+"F12.imprint","IMPRINT",EDGE,{"disambiguationData":[TD([[subQ1,1.0]])],"derivedFrom":subQ0}),makeQuery(id+"F12.imprint","IMPRINT",EDGE,{"disambiguationData":[TD([[makeQuery(id+"F12.imprint","INTERSECT",VERTEX,{"derivedFrom":[sQuery(id+"F12.wireOp",EDGE,"E5.right"),subQ0]}),1.0]])],"derivedFrom":subQ0})])],"isStart":true})});}
            var Q17;
            {var subQ0=sQuery(id+"F12.wireOp",EDGE,"E7.top");var subQ1=makeQuery(id+"F12.imprint","INTERSECT",VERTEX,{"derivedFrom":[makeQuery(id+"F8.boolean.opBoolean","COPY",EDGE,{"derivedFrom":makeQuery(id+"F8.opExtrude","CAP_EDGE",EDGE,{"disambiguationData":[OSD([sQuery(id+"F7.wireOp",EDGE,"E4.2")])],"isStart":true})}),subQ0]});Q17=makeQuery(id+"F13.boolean.opBoolean","COPY",EDGE,{"derivedFrom":makeQuery(id+"F13.opExtrude","CAP_EDGE",EDGE,{"disambiguationData":[OSD([subQ0]),TDD([makeQuery(id+"F12.imprint","IMPRINT",EDGE,{"disambiguationData":[TD([[subQ1,1.0]])],"derivedFrom":subQ0}),makeQuery(id+"F12.imprint","IMPRINT",EDGE,{"disambiguationData":[TD([[makeQuery(id+"F12.imprint","INTERSECT",VERTEX,{"derivedFrom":[sQuery(id+"F12.wireOp",EDGE,"E6.bottom"),subQ0]}),1.0]])],"derivedFrom":subQ0})])],"isStart":true})});}
            fillet(context, id + "F14", {"entities" : qUnion([Q0, Q1, Q2, Q3, Q4, Q5, Q6, Q7, Q8, Q9, Q10, Q11, Q12, Q13, Q14, Q15, Q16, Q17]), "radius" : 0.75 * mm, "tangentPropagation" : true, "allowEdgeOverflow" : false});
        }
        {
            var Q0;
            Q0=makeQuery(id+"F1.opExtrude","CAP_EDGE",EDGE,{"disambiguationData":[OSD([sQuery(id+"F0.wireOp",EDGE,"E0.1")])],"isStart":true});
            var Q1;
            Q1=makeQuery(id+"F4.boolean.opBoolean","COPY",EDGE,{"derivedFrom":makeQuery(id+"F4.opExtrude","CAP_EDGE",EDGE,{"disambiguationData":[OSD([sQuery(id+"F3.wireOp",EDGE,"E2.1")])],"isStart":false})});
            var Q2;
            {var subQ0=sQuery(id+"F0.wireOp",EDGE,"E0.2");var subQ1=sQuery(id+"F0.wireOp",EDGE,"E0.1");var subQ6=makeQuery(id+"F1.opExtrude","CAP_EDGE",EDGE,{"disambiguationData":[OSD([subQ1])],"isStart":false});Q2=makeQuery(id+"F13.boolean.opBoolean","SPLIT",EDGE,{"disambiguationData":[TD([makeQuery(id+"F2.opFillet","BLEND_FACE",FACE,{"disambiguationData":[OSD([subQ1,subQ0])]})])],"derivedFrom":subQ6});}
            var Q3;
            {var subQ0=sQuery(id+"F0.wireOp",EDGE,"E0.1");var subQ1=sQuery(id+"F0.wireOp",EDGE,"E0.0");var subQ6=makeQuery(id+"F1.opExtrude","CAP_EDGE",EDGE,{"disambiguationData":[OSD([subQ0])],"isStart":false});Q3=makeQuery(id+"F13.boolean.opBoolean","SPLIT",EDGE,{"disambiguationData":[TD([makeQuery(id+"F2.opFillet","BLEND_FACE",FACE,{"disambiguationData":[OSD([subQ1,subQ0])]})])],"derivedFrom":subQ6});}
            var Q4;
            {var subQ0=sQuery(id+"F0.wireOp",EDGE,"E0.0");var subQ1=sQuery(id+"F0.wireOp",EDGE,"E0.1");var subQ4=makeQuery(id+"F1.opExtrude","CAP_EDGE",EDGE,{"disambiguationData":[OSD([subQ0])],"isStart":false});Q4=makeQuery(id+"F13.boolean.opBoolean","SPLIT",EDGE,{"disambiguationData":[TD([makeQuery(id+"F2.opFillet","BLEND_FACE",FACE,{"disambiguationData":[OSD([subQ0,subQ1])]})])],"derivedFrom":subQ4});}
            var Q5;
            {var subQ0=sQuery(id+"F0.wireOp",EDGE,"E0.0");var subQ1=sQuery(id+"F0.wireOp",EDGE,"E0.2");var subQ4=makeQuery(id+"F1.opExtrude","CAP_EDGE",EDGE,{"disambiguationData":[OSD([subQ0])],"isStart":false});Q5=makeQuery(id+"F13.boolean.opBoolean","SPLIT",EDGE,{"disambiguationData":[TD([makeQuery(id+"F2.opFillet","BLEND_FACE",FACE,{"disambiguationData":[OSD([subQ0,subQ1])]})])],"derivedFrom":subQ4});}
            var Q6;
            {var subQ0=sQuery(id+"F0.wireOp",EDGE,"E0.2");var subQ1=sQuery(id+"F0.wireOp",EDGE,"E0.1");var subQ6=makeQuery(id+"F1.opExtrude","CAP_EDGE",EDGE,{"disambiguationData":[OSD([subQ0])],"isStart":false});Q6=makeQuery(id+"F13.boolean.opBoolean","SPLIT",EDGE,{"disambiguationData":[TD([makeQuery(id+"F2.opFillet","BLEND_FACE",FACE,{"disambiguationData":[OSD([subQ1,subQ0])]})])],"derivedFrom":subQ6});}
            var Q7;
            {var subQ0=sQuery(id+"F0.wireOp",EDGE,"E0.2");var subQ1=sQuery(id+"F0.wireOp",EDGE,"E0.0");var subQ6=makeQuery(id+"F1.opExtrude","CAP_EDGE",EDGE,{"disambiguationData":[OSD([subQ0])],"isStart":false});Q7=makeQuery(id+"F13.boolean.opBoolean","SPLIT",EDGE,{"disambiguationData":[TD([makeQuery(id+"F2.opFillet","BLEND_FACE",FACE,{"disambiguationData":[OSD([subQ1,subQ0])]})])],"derivedFrom":subQ6});}
            fillet(context, id + "F15", {"entities" : qUnion([Q0, Q1, Q2, Q3, Q4, Q5, Q6, Q7]), "radius" : 1 * mm, "tangentPropagation" : true, "allowEdgeOverflow" : false});
        }
        {
            var Q0;
            {var subQ0=sQuery(id+"F7.wireOp",EDGE,"E4.1");var subQ1=sQuery(id+"F7.wireOp",EDGE,"E4.2");Q0=makeQuery(id+"F8.boolean.opBoolean","COPY",EDGE,{"disambiguationData":[TD([makeQuery(id+"F1.opExtrude","CAP_FACE",FACE,{"disambiguationData":[OSD([sQuery(id+"F0.wireOp",EDGE,"E0.0"),sQuery(id+"F0.wireOp",EDGE,"E0.1"),sQuery(id+"F0.wireOp",EDGE,"E0.2")])],"isStart":true})])],"derivedFrom":makeQuery(id+"F8.opExtrude","SWEPT_EDGE",EDGE,{"disambiguationData":[OSD([subQ0,subQ1])]})});}
            var Q1;
            {var subQ0=sQuery(id+"F7.wireOp",EDGE,"E4.0");var subQ1=sQuery(id+"F7.wireOp",EDGE,"E4.2");Q1=makeQuery(id+"F8.boolean.opBoolean","COPY",EDGE,{"disambiguationData":[TD([makeQuery(id+"F1.opExtrude","CAP_FACE",FACE,{"disambiguationData":[OSD([sQuery(id+"F0.wireOp",EDGE,"E0.0"),sQuery(id+"F0.wireOp",EDGE,"E0.1"),sQuery(id+"F0.wireOp",EDGE,"E0.2")])],"isStart":true})])],"derivedFrom":makeQuery(id+"F8.opExtrude","SWEPT_EDGE",EDGE,{"disambiguationData":[OSD([subQ0,subQ1])]})});}
            var Q2;
            {var subQ0=sQuery(id+"F7.wireOp",EDGE,"E4.1");var subQ1=sQuery(id+"F7.wireOp",EDGE,"E4.0");Q2=makeQuery(id+"F8.boolean.opBoolean","COPY",EDGE,{"disambiguationData":[TD([makeQuery(id+"F1.opExtrude","CAP_FACE",FACE,{"disambiguationData":[OSD([sQuery(id+"F0.wireOp",EDGE,"E0.0"),sQuery(id+"F0.wireOp",EDGE,"E0.1"),sQuery(id+"F0.wireOp",EDGE,"E0.2")])],"isStart":true})])],"derivedFrom":makeQuery(id+"F8.opExtrude","SWEPT_EDGE",EDGE,{"disambiguationData":[OSD([subQ1,subQ0])]})});}
            fillet(context, id + "F16", {"entities" : qUnion([Q0, Q1, Q2]), "radius" : 3 * mm, "tangentPropagation" : true, "allowEdgeOverflow" : false});
        }
        {
            var Q0;
            Q0=makeQuery(id+"F8.boolean.opBoolean","INTERSECT",EDGE,{"derivedFrom":[makeQuery(id+"F6.boolean.opBoolean","COPY",FACE,{"derivedFrom":makeQuery(id+"F6.opExtrude","CAP_FACE",FACE,{"disambiguationData":[OSD([sQuery(id+"F5.wireOp",EDGE,"E3.0"),sQuery(id+"F5.wireOp",EDGE,"E3.1"),sQuery(id+"F5.wireOp",EDGE,"E3.2")])],"isStart":true})}),makeQuery(id+"F8.opExtrude","SWEPT_FACE",FACE,{"disambiguationData":[OSD([sQuery(id+"F7.wireOp",EDGE,"E4.0")])]})]});
            var Q1;
            Q1=makeQuery(id+"F8.boolean.opBoolean","COPY",EDGE,{"derivedFrom":makeQuery(id+"F8.opExtrude","TWEAK_EDGE",EDGE,{"derivedFrom":[makeQuery(id+"F1.opExtrude","CAP_FACE",FACE,{"disambiguationData":[OSD([sQuery(id+"F0.wireOp",EDGE,"E0.0"),sQuery(id+"F0.wireOp",EDGE,"E0.1"),sQuery(id+"F0.wireOp",EDGE,"E0.2")])],"isStart":true}),makeQuery(id+"F7.imprint","IMPRINT",EDGE,{"derivedFrom":sQuery(id+"F7.wireOp",EDGE,"E4.0")})]})});
            var Q2;
            {var subQ0=makeQuery(id+"F6.boolean.opBoolean","COPY",FACE,{"derivedFrom":makeQuery(id+"F6.opExtrude","CAP_FACE",FACE,{"disambiguationData":[OSD([sQuery(id+"F5.wireOp",EDGE,"E3.0"),sQuery(id+"F5.wireOp",EDGE,"E3.1"),sQuery(id+"F5.wireOp",EDGE,"E3.2")])],"isStart":false})});var subQ4=sQuery(id+"F7.wireOp",EDGE,"E4.0");var subQ5=makeQuery(id+"F8.opExtrude","SWEPT_FACE",FACE,{"disambiguationData":[OSD([subQ4])]});var subQ6=sQuery(id+"F12.wireOp",EDGE,"E5.left");var subQ7=makeQuery(id+"F8.boolean.opBoolean","COPY",EDGE,{"derivedFrom":makeQuery(id+"F8.opExtrude","CAP_EDGE",EDGE,{"disambiguationData":[OSD([subQ4])],"isStart":true})});var subQ8=makeQuery(id+"F12.imprint","INTERSECT",VERTEX,{"derivedFrom":[subQ7,subQ6]});var subQ9=sQuery(id+"F12.wireOp",EDGE,"E7.top");var subQ10=makeQuery(id+"F12.imprint","INTERSECT",VERTEX,{"derivedFrom":[subQ6,subQ9]});Q2=makeQuery(id+"F13.boolean.opBoolean","SPLIT",EDGE,{"disambiguationData":[TD([makeQuery(id+"F13.opExtrude","SWEPT_FACE",FACE,{"disambiguationData":[OSD([subQ6]),TDD([makeQuery(id+"F12.imprint","IMPRINT",EDGE,{"disambiguationData":[TD([[subQ10,-1.0]])],"derivedFrom":subQ6}),makeQuery(id+"F12.imprint","IMPRINT",EDGE,{"disambiguationData":[TD([[subQ8,-1.0]])],"derivedFrom":subQ6})])]})])],"derivedFrom":makeQuery(id+"F8.boolean.opBoolean","INTERSECT",EDGE,{"derivedFrom":[subQ0,subQ5]})});}
            var Q3;
            {var subQ3=sQuery(id+"F7.wireOp",EDGE,"E4.1");var subQ4=sQuery(id+"F12.wireOp",EDGE,"E7.bottom");var subQ5=sQuery(id+"F12.wireOp",EDGE,"E6.top");var subQ6=makeQuery(id+"F12.imprint","INTERSECT",VERTEX,{"derivedFrom":[subQ5,subQ4]});var subQ7=makeQuery(id+"F8.boolean.opBoolean","COPY",EDGE,{"derivedFrom":makeQuery(id+"F8.opExtrude","CAP_EDGE",EDGE,{"disambiguationData":[OSD([subQ3])],"isStart":true})});var subQ8=makeQuery(id+"F12.imprint","INTERSECT",VERTEX,{"derivedFrom":[subQ7,subQ5]});Q3=makeQuery(id+"F13.boolean.opBoolean","SPLIT",EDGE,{"disambiguationData":[TD([makeQuery(id+"F13.opExtrude","SWEPT_FACE",FACE,{"disambiguationData":[OSD([subQ5]),TDD([makeQuery(id+"F12.imprint","IMPRINT",EDGE,{"disambiguationData":[TD([[subQ8,1.0]])],"derivedFrom":subQ5}),makeQuery(id+"F12.imprint","IMPRINT",EDGE,{"disambiguationData":[TD([[subQ6,1.0]])],"derivedFrom":subQ5})])]})])],"derivedFrom":subQ7});}
            var Q4;
            {var subQ3=sQuery(id+"F7.wireOp",EDGE,"E4.0");var subQ4=sQuery(id+"F12.wireOp",EDGE,"E6.top");var subQ6=makeQuery(id+"F8.boolean.opBoolean","COPY",EDGE,{"derivedFrom":makeQuery(id+"F8.opExtrude","CAP_EDGE",EDGE,{"disambiguationData":[OSD([subQ3])],"isStart":true})});var subQ8=sQuery(id+"F12.wireOp",EDGE,"E5.right");var subQ9=makeQuery(id+"F12.imprint","INTERSECT",VERTEX,{"derivedFrom":[subQ8,subQ4]});var subQ10=makeQuery(id+"F12.imprint","INTERSECT",VERTEX,{"derivedFrom":[subQ6,subQ8]});Q4=makeQuery(id+"F13.boolean.opBoolean","SPLIT",EDGE,{"disambiguationData":[TD([makeQuery(id+"F13.opExtrude","SWEPT_FACE",FACE,{"disambiguationData":[OSD([subQ8]),TDD([makeQuery(id+"F12.imprint","IMPRINT",EDGE,{"disambiguationData":[TD([[subQ9,-1.0]])],"derivedFrom":subQ8}),makeQuery(id+"F12.imprint","IMPRINT",EDGE,{"disambiguationData":[TD([[subQ10,-1.0]])],"derivedFrom":subQ8})])]})])],"derivedFrom":subQ6});}
            var Q5;
            {var subQ3=sQuery(id+"F12.wireOp",EDGE,"E6.bottom");var subQ5=sQuery(id+"F7.wireOp",EDGE,"E4.2");var subQ6=makeQuery(id+"F8.boolean.opBoolean","COPY",EDGE,{"derivedFrom":makeQuery(id+"F8.opExtrude","CAP_EDGE",EDGE,{"disambiguationData":[OSD([subQ5])],"isStart":true})});var subQ8=sQuery(id+"F12.wireOp",EDGE,"E7.top");var subQ9=makeQuery(id+"F12.imprint","INTERSECT",VERTEX,{"derivedFrom":[subQ3,subQ8]});var subQ10=makeQuery(id+"F12.imprint","INTERSECT",VERTEX,{"derivedFrom":[subQ6,subQ8]});Q5=makeQuery(id+"F13.boolean.opBoolean","SPLIT",EDGE,{"disambiguationData":[TD([makeQuery(id+"F13.opExtrude","SWEPT_FACE",FACE,{"disambiguationData":[OSD([subQ8]),TDD([makeQuery(id+"F12.imprint","IMPRINT",EDGE,{"disambiguationData":[TD([[subQ10,1.0]])],"derivedFrom":subQ8}),makeQuery(id+"F12.imprint","IMPRINT",EDGE,{"disambiguationData":[TD([[subQ9,1.0]])],"derivedFrom":subQ8})])]})])],"derivedFrom":subQ6});}
            var Q6;
            {var subQ3=sQuery(id+"F7.wireOp",EDGE,"E4.1");var subQ4=sQuery(id+"F12.wireOp",EDGE,"E6.bottom");var subQ5=sQuery(id+"F12.wireOp",EDGE,"E5.left");var subQ6=makeQuery(id+"F12.imprint","INTERSECT",VERTEX,{"derivedFrom":[subQ5,subQ4]});var subQ7=makeQuery(id+"F8.boolean.opBoolean","COPY",EDGE,{"derivedFrom":makeQuery(id+"F8.opExtrude","CAP_EDGE",EDGE,{"disambiguationData":[OSD([subQ3])],"isStart":true})});var subQ10=makeQuery(id+"F12.imprint","INTERSECT",VERTEX,{"derivedFrom":[subQ7,subQ4]});Q6=makeQuery(id+"F13.boolean.opBoolean","SPLIT",EDGE,{"disambiguationData":[TD([makeQuery(id+"F13.opExtrude","SWEPT_FACE",FACE,{"disambiguationData":[OSD([subQ4]),TDD([makeQuery(id+"F12.imprint","IMPRINT",EDGE,{"disambiguationData":[TD([[subQ10,1.0]])],"derivedFrom":subQ4}),makeQuery(id+"F12.imprint","IMPRINT",EDGE,{"disambiguationData":[TD([[subQ6,1.0]])],"derivedFrom":subQ4})])]})])],"derivedFrom":subQ7});}
            var Q7;
            {var subQ3=sQuery(id+"F12.wireOp",EDGE,"E7.bottom");var subQ4=sQuery(id+"F12.wireOp",EDGE,"E5.right");var subQ5=makeQuery(id+"F12.imprint","INTERSECT",VERTEX,{"derivedFrom":[subQ4,subQ3]});var subQ6=sQuery(id+"F7.wireOp",EDGE,"E4.2");var subQ7=makeQuery(id+"F8.boolean.opBoolean","COPY",EDGE,{"derivedFrom":makeQuery(id+"F8.opExtrude","CAP_EDGE",EDGE,{"disambiguationData":[OSD([subQ6])],"isStart":true})});var subQ10=makeQuery(id+"F12.imprint","INTERSECT",VERTEX,{"derivedFrom":[subQ7,subQ3]});Q7=makeQuery(id+"F13.boolean.opBoolean","SPLIT",EDGE,{"disambiguationData":[TD([makeQuery(id+"F13.opExtrude","SWEPT_FACE",FACE,{"disambiguationData":[OSD([subQ3]),TDD([makeQuery(id+"F12.imprint","IMPRINT",EDGE,{"disambiguationData":[TD([[subQ10,1.0]])],"derivedFrom":subQ3}),makeQuery(id+"F12.imprint","IMPRINT",EDGE,{"disambiguationData":[TD([[subQ5,1.0]])],"derivedFrom":subQ3})])]})])],"derivedFrom":subQ7});}
            fillet(context, id + "F17", {"entities" : qUnion([Q0, Q1, Q2, Q3, Q4, Q5, Q6, Q7]), "radius" : 1 * mm, "tangentPropagation" : true, "allowEdgeOverflow" : false});
        }
    });
